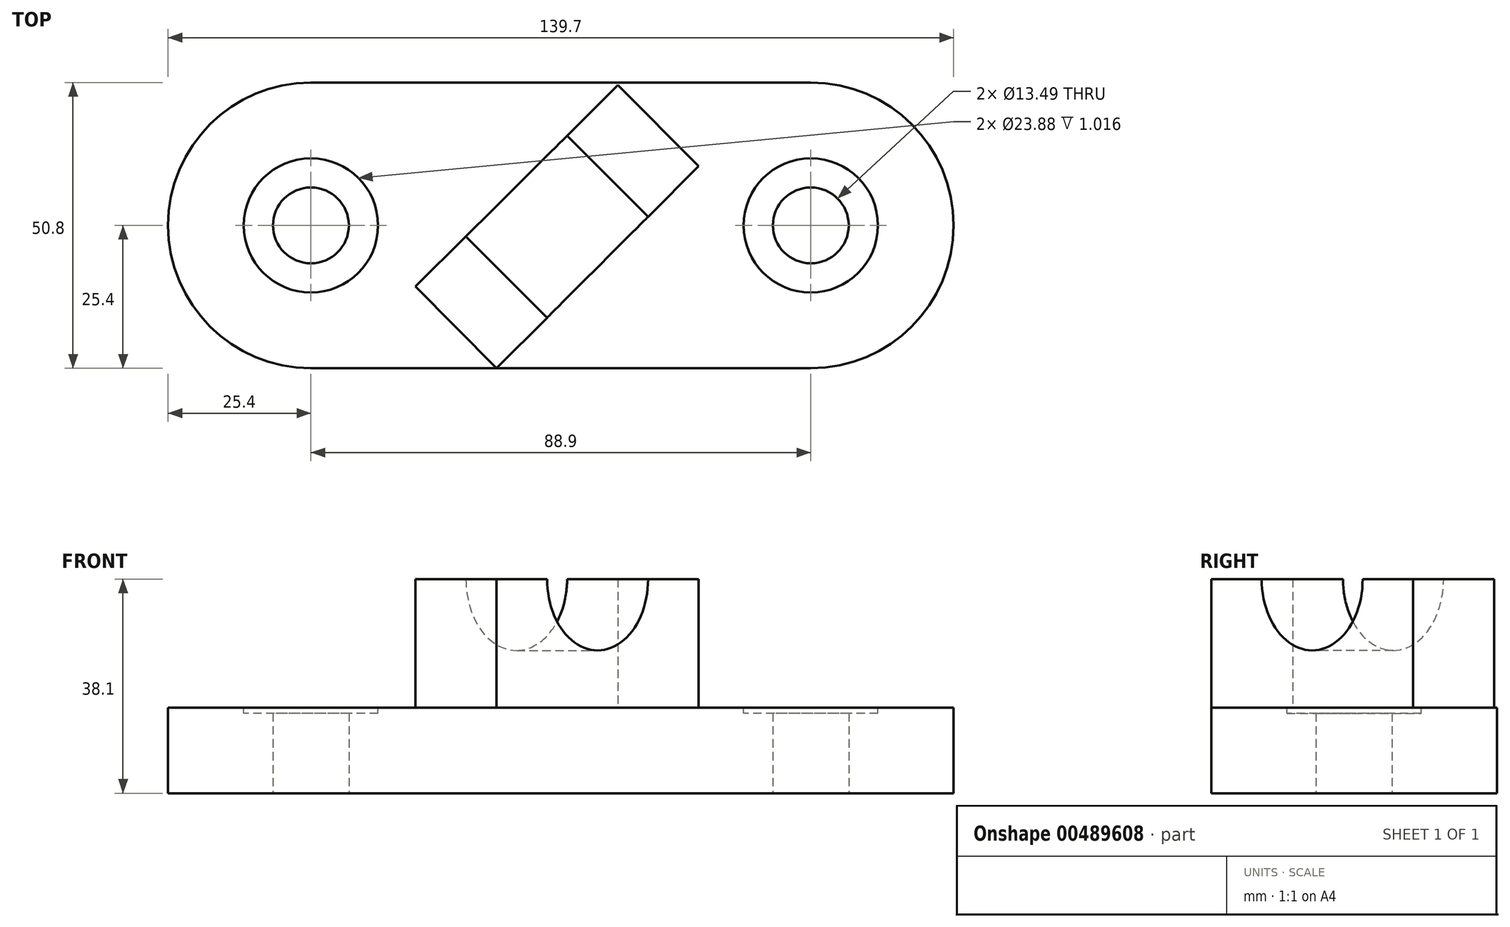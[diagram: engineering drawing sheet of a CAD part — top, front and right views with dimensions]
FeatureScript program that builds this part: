
annotation { "Feature Type Name" : "Feature", "Feature Type Description" : "" }
export const myFeature = defineFeature(function(context is Context, id is Id, definition is map)
    precondition{}
    {
        {
            var Q0;
            Q0=qCreatedBy(makeId("Top.planeOp"),FACE);
            var sketch = newSketch(context, id + "F0", { "sketchPlane" : qUnion([Q0])});
            skLineSegment(sketch, "E0.bottom", {"start": v(44.45, 25.4) * mm, "end": v(-44.45, 25.4) * mm});
            skLineSegment(sketch, "E0.top", {"start": v(44.45, -25.4) * mm, "end": v(-44.45, -25.4) * mm});
            skPoint(sketch, "E0.middle", {"position": v(0, 0) * mm});
            skArc(sketch, "E1", {"start": v(44.45, 25.4) * mm, "mid": v(69.85, 0) * mm, "end": v(44.45, -25.4) * mm});
            skArc(sketch, "E2", {"start": v(-44.45, 25.4) * mm, "mid": v(-69.85, 0) * mm, "end": v(-44.45, -25.4) * mm});
            skCircle(sketch, "E3", {"center": v(44.45, 0) * mm, "radius": 6.74 * mm});
            skCircle(sketch, "E4", {"center": v(-44.45, 0) * mm, "radius": 6.74 * mm});
            skPoint(sketch, "E5", {"position": v(-11.43, -25.4) * mm});
            skLineSegment(sketch, "E6", {"start": v(-11.43, -25.4) * mm, "end": v(24.5, 10.52) * mm});
            skLineSegment(sketch, "E7", {"start": v(24.5, 10.52) * mm, "end": v(10.17, 24.94) * mm});
            skLineSegment(sketch, "E8", {"start": v(10.17, 24.94) * mm, "end": v(-25.87, -10.87) * mm});
            skLineSegment(sketch, "E9", {"start": v(-25.87, -10.87) * mm, "end": v(-11.43, -25.4) * mm});
            skSolve(sketch);
        }
        {
            var Q0;
            Q0 = qSketchRegion(id + "F0", true);
            var Q1;
            Q1 = qSketchRegion(id + "F10", true);
            extrude(context, id + "F1", {"entities" : qUnion([Q0, Q1]), "depth" : 15.24 * mm});
        }
        {
            var Q0;
            Q0=makeQuery(id+"F1.opExtrude","CAP_FACE",FACE,{"disambiguationData":[OSD([sQuery(id+"F0.wireOp",EDGE,"E0.bottom"),sQuery(id+"F0.wireOp",EDGE,"E0.top"),sQuery(id+"F0.wireOp",EDGE,"E1"),sQuery(id+"F0.wireOp",EDGE,"E2"),sQuery(id+"F0.wireOp",EDGE,"E3"),sQuery(id+"F0.wireOp",EDGE,"E4")])],"isStart":false});
            var sketch = newSketch(context, id + "F2", { "sketchPlane" : qUnion([Q0])});
            skCircle(sketch, "E10", {"center": v(-44.45, 0) * mm, "radius": 11.94 * mm});
            skCircle(sketch, "E11", {"center": v(44.45, 0) * mm, "radius": 11.94 * mm});
            skSolve(sketch);
        }
        {
            var Q0;
            Q0=makeQuery(id+"F0.imprint","IMPRINT",FACE,{"disambiguationData":[TD([[makeQuery(id+"F0.imprint","IMPRINT",EDGE,{"derivedFrom":sQuery(id+"F0.wireOp",EDGE,"E6")}),1.0]])]});
            extrude(context, id + "F3", {"entities" : qUnion([Q0]), "operationType" : NewBodyOperationType.ADD, "depth" : 38.1 * mm});
        }
        {
            var Q0;
            Q0=makeQuery(id+"F2.imprint","IMPRINT",FACE,{"disambiguationData":[TD([[makeQuery(id+"F2.imprint","IMPRINT",EDGE,{"derivedFrom":sQuery(id+"F2.wireOp",EDGE,"E11")}),1.0]])]});
            extrude(context, id + "F4", {"entities" : qUnion([Q0]), "operationType" : NewBodyOperationType.REMOVE, "oppositeDirection" : true, "depth" : 1.02 * mm});
        }
        {
            var Q0;
            Q0=makeQuery(id+"F2.imprint","IMPRINT",FACE,{"disambiguationData":[TD([[makeQuery(id+"F2.imprint","IMPRINT",EDGE,{"derivedFrom":sQuery(id+"F2.wireOp",EDGE,"E10")}),1.0]])]});
            extrude(context, id + "F5", {"entities" : qUnion([Q0]), "operationType" : NewBodyOperationType.REMOVE, "oppositeDirection" : true, "depth" : 1.02 * mm});
        }
        {
            var Q0;
            Q0=makeQuery(id+"F3.opExtrude","SWEPT_FACE",FACE,{"disambiguationData":[OSD([sQuery(id+"F0.wireOp",EDGE,"E6")])]});
            var sketch = newSketch(context, id + "F6", { "sketchPlane" : qUnion([Q0])});
            skArc(sketch, "E12", {"start": v(-26.04, 38.1) * mm, "mid": v(-0.64, 63.5) * mm, "end": v(24.76, 38.1) * mm});
            skCircle(sketch, "E13", {"center": v(-0.64, 38.1) * mm, "radius": 12.7 * mm});
            skSolve(sketch);
        }
        {
            var Q0;
            Q0 = qSketchRegion(id + "F6", true);
            var Q1;
            {var subQ0=sQuery(id+"F6.wireOp",EDGE,"E12");Q1=makeQuery(id+"F6.imprint","IMPRINT",FACE,{"disambiguationData":[TD([[makeQuery(id+"F6.imprint","IMPRINT",EDGE,{"derivedFrom":subQ0}),-1.0]])]});}
            var Q2;
            Q2=makeQuery(id+"F3.opExtrude","SWEPT_FACE",FACE,{"disambiguationData":[OSD([sQuery(id+"F0.wireOp",EDGE,"E8")])]});
            extrude(context, id + "F7", {"entities" : qUnion([Q0, Q1]), "operationType" : NewBodyOperationType.ADD, "endBound" : BoundingType.UP_TO_SURFACE, "oppositeDirection" : true, "endBoundEntityFace" : qUnion([Q2]), "depth" : 20.32 * mm});
        }
        {
            var Q0;
            {var subQ0=sQuery(id+"F6.wireOp",EDGE,"E13");var subQ1=makeQuery(id+"F3.opExtrude","CAP_EDGE",EDGE,{"disambiguationData":[OSD([sQuery(id+"F0.wireOp",EDGE,"E6")])],"isStart":false});var subQ2=makeQuery(id+"F6.imprint","INTERSECT",VERTEX,{"disambiguationData":[OD(0.0)],"derivedFrom":[subQ1,subQ0]});Q0=makeQuery(id+"F6.imprint","IMPRINT",FACE,{"disambiguationData":[TD([[makeQuery(id+"F6.imprint","IMPRINT",EDGE,{"disambiguationData":[TD([[subQ2,1.0]])],"derivedFrom":subQ0}),1.0]])]});}
            var Q1;
            {var subQ0=sQuery(id+"F6.wireOp",EDGE,"E13");var subQ1=makeQuery(id+"F3.opExtrude","CAP_EDGE",EDGE,{"disambiguationData":[OSD([sQuery(id+"F0.wireOp",EDGE,"E6")])],"isStart":false});var subQ2=makeQuery(id+"F6.imprint","INTERSECT",VERTEX,{"disambiguationData":[OD(0.0)],"derivedFrom":[subQ1,subQ0]});Q1=makeQuery(id+"F6.imprint","IMPRINT",FACE,{"disambiguationData":[TD([[makeQuery(id+"F6.imprint","IMPRINT",EDGE,{"disambiguationData":[TD([[subQ2,-1.0]])],"derivedFrom":subQ0}),1.0]])]});}
            extrude(context, id + "F8", {"entities" : qUnion([Q0, Q1]), "operationType" : NewBodyOperationType.REMOVE, "endBound" : BoundingType.THROUGH_ALL, "oppositeDirection" : true, "depth" : 25.4 * mm});
        }
        {
            var Q0;
            Q0=qCreatedBy(makeId("Top.planeOp"),FACE);
            cPlane(context, id + "F9", {"entities" : qUnion([Q0]), "cplaneType" : CPlaneType.OFFSET, "offset" : 63.5 * mm, "width" : 152.4 * mm, "height" : 152.4 * mm});
        }
        {
            var Q0;
            Q0=qCreatedBy(id+"F9.planeOp",FACE);
            var sketch = newSketch(context, id + "F10", { "sketchPlane" : qUnion([Q0])});
            skCircle(sketch, "E14", {"center": v(0, 0) * mm, "radius": 1.59 * mm});
            skSolve(sketch);
        }
        {
            var Q0;
            Q0=makeQuery(id+"F10.imprint","IMPRINT",FACE,{"disambiguationData":[TD([[makeQuery(id+"F10.imprint","IMPRINT",EDGE,{"derivedFrom":sQuery(id+"F10.wireOp",EDGE,"E14")}),1.0]])]});
            extrude(context, id + "F11", {"entities" : qUnion([Q0]), "operationType" : NewBodyOperationType.REMOVE, "oppositeDirection" : true, "depth" : 25.4 * mm});
        }
    });
